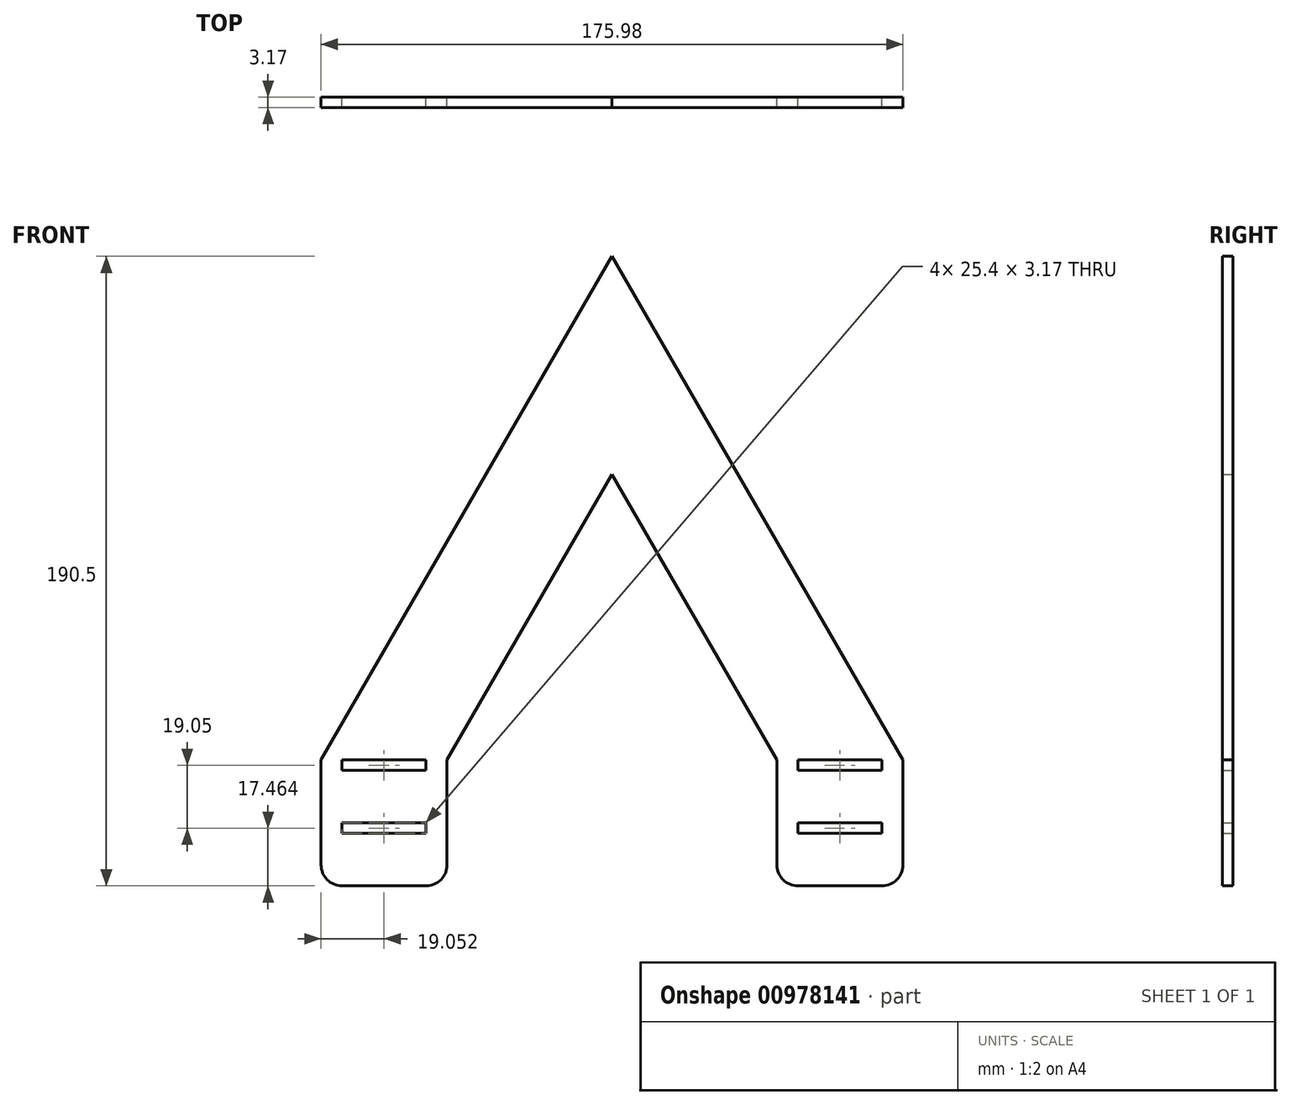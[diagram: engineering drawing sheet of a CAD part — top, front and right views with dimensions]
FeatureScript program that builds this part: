
annotation { "Feature Type Name" : "Feature", "Feature Type Description" : "" }
export const myFeature = defineFeature(function(context is Context, id is Id, definition is map)
    precondition{}
    {
        {
            var Q0;
            Q0=qCreatedBy(makeId("Front.planeOp"),FACE);
            var sketch = newSketch(context, id + "F0", { "sketchPlane" : qUnion([Q0])});
            skLineSegment(sketch, "E0", {"start": v(0, 0) * mm, "end": v(-49.89, -86.4) * mm});
            skLineSegment(sketch, "E1", {"start": v(-49.89, -86.4) * mm, "end": v(-87.99, -86.4) * mm, "construction": true});
            skLineSegment(sketch, "E2", {"start": v(-87.99, -86.4) * mm, "end": v(0, 66) * mm});
            skLineSegment(sketch, "E3", {"start": v(0, 66) * mm, "end": v(87.99, -86.4) * mm});
            skLineSegment(sketch, "E4", {"start": v(87.99, -86.4) * mm, "end": v(49.89, -86.4) * mm, "construction": true});
            skLineSegment(sketch, "E5", {"start": v(49.89, -86.4) * mm, "end": v(0, 0) * mm});
            skLineSegment(sketch, "E6", {"start": v(-49.89, -86.4) * mm, "end": v(0, -86.4) * mm, "construction": true});
            skLineSegment(sketch, "E7", {"start": v(0, -86.4) * mm, "end": v(49.89, -86.4) * mm, "construction": true});
            skLineSegment(sketch, "E8.left", {"start": v(-49.89, -86.4) * mm, "end": v(-49.89, -86.4) * mm});
            skLineSegment(sketch, "E8.right", {"start": v(-87.99, -86.4) * mm, "end": v(-87.99, -86.4) * mm});
            skLineSegment(sketch, "E9.top", {"start": v(-49.89, -105.46) * mm, "end": v(-87.99, -105.46) * mm, "construction": true});
            skLineSegment(sketch, "E9.left", {"start": v(-49.89, -86.4) * mm, "end": v(-49.89, -105.46) * mm});
            skLineSegment(sketch, "E9.right", {"start": v(-87.99, -86.4) * mm, "end": v(-87.99, -105.46) * mm});
            skLineSegment(sketch, "E10.bottom", {"start": v(49.89, -86.4) * mm, "end": v(87.99, -86.4) * mm, "construction": true});
            skLineSegment(sketch, "E10.top", {"start": v(49.89, -105.46) * mm, "end": v(87.99, -105.46) * mm, "construction": true});
            skLineSegment(sketch, "E10.left", {"start": v(49.89, -86.4) * mm, "end": v(49.89, -105.46) * mm});
            skLineSegment(sketch, "E10.right", {"start": v(87.99, -86.4) * mm, "end": v(87.99, -105.46) * mm});
            skLineSegment(sketch, "E11.top", {"start": v(56.24, -124.5) * mm, "end": v(81.64, -124.5) * mm});
            skLineSegment(sketch, "E11.left", {"start": v(49.89, -105.46) * mm, "end": v(49.89, -118.16) * mm});
            skLineSegment(sketch, "E11.right", {"start": v(87.99, -105.46) * mm, "end": v(87.99, -118.16) * mm});
            skLineSegment(sketch, "E12.top", {"start": v(-56.24, -124.5) * mm, "end": v(-81.64, -124.5) * mm});
            skLineSegment(sketch, "E12.left", {"start": v(-49.89, -105.46) * mm, "end": v(-49.89, -118.16) * mm});
            skLineSegment(sketch, "E12.right", {"start": v(-87.99, -105.46) * mm, "end": v(-87.99, -118.16) * mm});
            skLineSegment(sketch, "E13.bottom", {"start": v(-81.64, -86.4) * mm, "end": v(-56.24, -86.4) * mm});
            skLineSegment(sketch, "E13.top", {"start": v(-81.64, -89.58) * mm, "end": v(-56.24, -89.58) * mm});
            skLineSegment(sketch, "E13.left", {"start": v(-81.64, -86.4) * mm, "end": v(-81.64, -89.58) * mm});
            skLineSegment(sketch, "E13.right", {"start": v(-56.24, -86.4) * mm, "end": v(-56.24, -89.58) * mm});
            skLineSegment(sketch, "E14.bottom", {"start": v(56.24, -86.4) * mm, "end": v(81.64, -86.4) * mm});
            skLineSegment(sketch, "E14.top", {"start": v(56.24, -89.58) * mm, "end": v(81.64, -89.58) * mm});
            skLineSegment(sketch, "E14.left", {"start": v(56.24, -86.4) * mm, "end": v(56.24, -89.58) * mm});
            skLineSegment(sketch, "E14.right", {"start": v(81.64, -86.4) * mm, "end": v(81.64, -89.58) * mm});
            skLineSegment(sketch, "E15.bottom", {"start": v(-81.64, -105.46) * mm, "end": v(-56.24, -105.46) * mm});
            skLineSegment(sketch, "E15.top", {"start": v(-81.64, -108.63) * mm, "end": v(-56.24, -108.63) * mm});
            skLineSegment(sketch, "E15.left", {"start": v(-81.64, -105.46) * mm, "end": v(-81.64, -108.63) * mm});
            skLineSegment(sketch, "E15.right", {"start": v(-56.24, -105.46) * mm, "end": v(-56.24, -108.63) * mm});
            skLineSegment(sketch, "E16.bottom", {"start": v(56.24, -105.46) * mm, "end": v(81.64, -105.46) * mm});
            skLineSegment(sketch, "E16.top", {"start": v(56.24, -108.63) * mm, "end": v(81.64, -108.63) * mm});
            skLineSegment(sketch, "E16.left", {"start": v(56.24, -105.46) * mm, "end": v(56.24, -108.63) * mm});
            skLineSegment(sketch, "E16.right", {"start": v(81.64, -105.46) * mm, "end": v(81.64, -108.63) * mm});
            skPoint(sketch, "E17.visualSharp", {"position": v(49.89, -124.5) * mm});
            skArc(sketch, "E17.filletArc", {"start": v(49.89, -118.16) * mm, "mid": v(51.75, -122.65) * mm, "end": v(56.24, -124.5) * mm});
            skPoint(sketch, "E18.visualSharp", {"position": v(87.99, -124.5) * mm});
            skArc(sketch, "E18.filletArc", {"start": v(81.64, -124.5) * mm, "mid": v(86.13, -122.65) * mm, "end": v(87.99, -118.16) * mm});
            skPoint(sketch, "E19.visualSharp", {"position": v(-49.89, -124.5) * mm});
            skArc(sketch, "E19.filletArc", {"start": v(-56.24, -124.5) * mm, "mid": v(-51.75, -122.65) * mm, "end": v(-49.89, -118.16) * mm});
            skPoint(sketch, "E20.visualSharp", {"position": v(-87.99, -124.5) * mm});
            skArc(sketch, "E20.filletArc", {"start": v(-87.99, -118.16) * mm, "mid": v(-86.13, -122.65) * mm, "end": v(-81.64, -124.5) * mm});
            skSolve(sketch);
        }
        {
            var Q0;
            Q0 = qSketchRegion(id + "F0", true);
            extrude(context, id + "F1", {"entities" : qUnion([Q0]), "depth" : 3.17 * mm, "offsetDistance" : 25.4 * mm});
        }
    });
